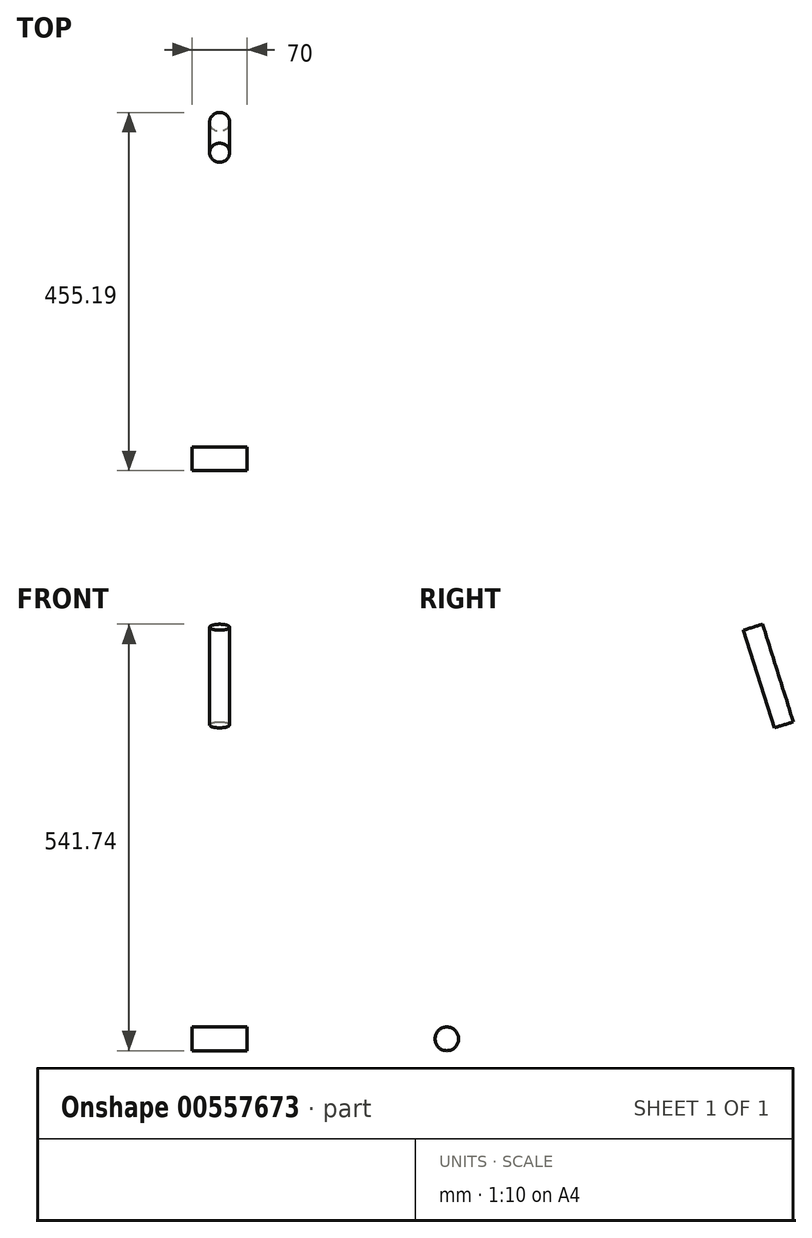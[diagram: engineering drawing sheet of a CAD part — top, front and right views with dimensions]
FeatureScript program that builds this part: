
annotation { "Feature Type Name" : "Feature", "Feature Type Description" : "" }
export const myFeature = defineFeature(function(context is Context, id is Id, definition is map)
    precondition{}
    {
        {
            var Q0;
            Q0=qCreatedBy(makeId("Right.planeOp"),FACE);
            var sketch = newSketch(context, id + "F0", { "sketchPlane" : qUnion([Q0])});
            skPoint(sketch, "E0", {"position": v(0, 271.5) * mm});
            skPoint(sketch, "E1", {"position": v(-375.23, 331.5) * mm});
            skPoint(sketch, "E2", {"position": v(576.89, 331.5) * mm});
            skCircle(sketch, "E3", {"center": v(-375.23, 331.5) * mm, "radius": 331.5 * mm});
            skCircle(sketch, "E4", {"center": v(576.89, 331.5) * mm, "radius": 331.5 * mm});
            skLineSegment(sketch, "E5", {"start": v(-873.64, 0) * mm, "end": v(1243.72, 0) * mm, "construction": true});
            skLineSegment(sketch, "E6", {"start": v(0, 0) * mm, "end": v(0, 1098.11) * mm, "construction": true});
            skLineSegment(sketch, "E7", {"start": v(-375.23, 331.5) * mm, "end": v(576.89, 331.5) * mm, "construction": true});
            skLineSegment(sketch, "E8", {"start": v(-50, 1099.43) * mm, "end": v(-50, 0) * mm, "construction": true});
            skLineSegment(sketch, "E9", {"start": v(850, 0) * mm, "end": v(850, 1102.57) * mm, "construction": true});
            skLineSegment(sketch, "E10", {"start": v(800, 0) * mm, "end": v(800, 1098.19) * mm, "construction": true});
            skLineSegment(sketch, "E11", {"start": v(750, 0) * mm, "end": v(750, 1136.17) * mm, "construction": true});
            skCircle(sketch, "E12", {"center": v(0, 271.5) * mm, "radius": 170 * mm});
            skLineSegment(sketch, "E13", {"start": v(-50, 970) * mm, "end": v(-290, 970) * mm});
            skLineSegment(sketch, "E14", {"start": v(388.99, 794.42) * mm, "end": v(639.47, 0) * mm});
            skLineSegment(sketch, "E15", {"start": v(358.03, 648.35) * mm, "end": v(482.66, 687.65) * mm});
            skPoint(sketch, "E16", {"position": v(800, 955) * mm});
            skLineSegment(sketch, "E17", {"start": v(800, 955) * mm, "end": v(454.17, 855) * mm});
            skLineSegment(sketch, "E18", {"start": v(524.17, 855) * mm, "end": v(454.17, 855) * mm});
            skLineSegment(sketch, "E19", {"start": v(477.13, 848) * mm, "end": v(547.13, 848) * mm});
            skLineSegment(sketch, "E20", {"start": v(800, 948) * mm, "end": v(477.13, 848) * mm});
            skLineSegment(sketch, "E21", {"start": v(-50, 1060) * mm, "end": v(-290, 1060) * mm});
            skPoint(sketch, "E22", {"position": v(428.08, 670.44) * mm});
            skSolve(sketch);
        }
        {
            var Q0;
            Q0=qCreatedBy(makeId("Right.planeOp"),FACE);
            var sketch = newSketch(context, id + "F1", { "sketchPlane" : qUnion([Q0])});
            skLineSegment(sketch, "E23", {"start": v(369.24, 652.29) * mm, "end": v(442.39, 684.68) * mm});
            skLineSegment(sketch, "E24", {"start": v(442.39, 684.68) * mm, "end": v(603.27, 321.3) * mm});
            skLineSegment(sketch, "E25", {"start": v(603.27, 321.3) * mm, "end": v(530.12, 288.92) * mm});
            skLineSegment(sketch, "E26", {"start": v(530.12, 288.92) * mm, "end": v(369.24, 652.29) * mm});
            skLineSegment(sketch, "E27", {"start": v(-57.53, 264) * mm, "end": v(353.83, 689.76) * mm});
            skLineSegment(sketch, "E28", {"start": v(411.37, 634.18) * mm, "end": v(353.83, 689.76) * mm});
            skLineSegment(sketch, "E29", {"start": v(411.37, 634.18) * mm, "end": v(0, 208.41) * mm});
            skLineSegment(sketch, "E30", {"start": v(0, 208.41) * mm, "end": v(-57.53, 264) * mm});
            skLineSegment(sketch, "E31", {"start": v(24.66, 216.42) * mm, "end": v(36.44, 295.55) * mm});
            skLineSegment(sketch, "E32", {"start": v(36.44, 295.55) * mm, "end": v(-430.88, 365.14) * mm});
            skLineSegment(sketch, "E33", {"start": v(-430.88, 365.14) * mm, "end": v(-442.67, 286.02) * mm});
            skLineSegment(sketch, "E34", {"start": v(-442.67, 286.02) * mm, "end": v(24.66, 216.42) * mm});
            skLineSegment(sketch, "E35", {"start": v(-97.86, 702.11) * mm, "end": v(-392.56, 270.67) * mm});
            skLineSegment(sketch, "E36", {"start": v(-458.62, 315.8) * mm, "end": v(-392.56, 270.67) * mm});
            skLineSegment(sketch, "E37", {"start": v(-163.91, 747.23) * mm, "end": v(-97.86, 702.11) * mm});
            skLineSegment(sketch, "E38", {"start": v(-163.91, 747.23) * mm, "end": v(-458.62, 315.8) * mm});
            skLineSegment(sketch, "E39", {"start": v(-19.5, 202.08) * mm, "end": v(56.58, 226.8) * mm});
            skLineSegment(sketch, "E40", {"start": v(56.58, 226.8) * mm, "end": v(-150, 862.6) * mm});
            skLineSegment(sketch, "E41", {"start": v(-150, 862.6) * mm, "end": v(-226.08, 837.87) * mm});
            skLineSegment(sketch, "E42", {"start": v(-226.08, 837.87) * mm, "end": v(-19.5, 202.08) * mm});
            skPoint(sketch, "E43.0", {"position": v(0, 271.5) * mm});
            skLineSegment(sketch, "E44", {"start": v(327, 774.88) * mm, "end": v(366.09, 650.9) * mm});
            skLineSegment(sketch, "E45", {"start": v(366.09, 650.9) * mm, "end": v(442.39, 674.95) * mm});
            skLineSegment(sketch, "E46", {"start": v(442.39, 674.95) * mm, "end": v(403.3, 798.93) * mm});
            skLineSegment(sketch, "E47", {"start": v(403.3, 798.93) * mm, "end": v(327, 774.88) * mm});
            skLineSegment(sketch, "E48.0", {"start": v(-50, 970) * mm, "end": v(-290, 970) * mm, "construction": true});
            skPoint(sketch, "E49", {"position": v(-150, 970) * mm});
            skLineSegment(sketch, "E50.bottom", {"start": v(-110, 970) * mm, "end": v(-190, 970) * mm});
            skLineSegment(sketch, "E50.top", {"start": v(-110, 782.11) * mm, "end": v(-190, 782.11) * mm});
            skLineSegment(sketch, "E50.left", {"start": v(-110, 970) * mm, "end": v(-110, 782.11) * mm});
            skLineSegment(sketch, "E50.right", {"start": v(-190, 970) * mm, "end": v(-190, 782.11) * mm});
            skPoint(sketch, "E51", {"position": v(-150, 782.11) * mm});
            skPoint(sketch, "E52.0", {"position": v(576.89, 331.5) * mm});
            skCircle(sketch, "E53", {"center": v(576.89, 331.5) * mm, "radius": 336.5 * mm, "construction": true});
            skPoint(sketch, "E54", {"position": v(387.97, 609.97) * mm});
            skPoint(sketch, "E55.0", {"position": v(-375.23, 331.5) * mm});
            skCircle(sketch, "E56", {"center": v(-375.23, 331.5) * mm, "radius": 336.5 * mm, "construction": true});
            skLineSegment(sketch, "E57", {"start": v(27.6, 236.2) * mm, "end": v(-433.83, 345.36) * mm, "construction": true});
            skPoint(sketch, "E57.startSnap0", {"position": v(-28.77, 236.2) * mm});
            skLineSegment(sketch, "E58", {"start": v(-114.37, 713.4) * mm, "end": v(-409.08, 281.96) * mm, "construction": true});
            skLineSegment(sketch, "E59", {"start": v(266.06, 702.11) * mm, "end": v(290.59, 624.3) * mm});
            skLineSegment(sketch, "E60", {"start": v(-73.13, 626.03) * mm, "end": v(-17.86, 702.11) * mm});
            skLineSegment(sketch, "E61", {"start": v(-5.9, 419.1) * mm, "end": v(74.4, 400.56) * mm});
            skLineSegment(sketch, "E62", {"start": v(-199.98, 552.6) * mm, "end": v(-130.14, 542.58) * mm});
            skLineSegment(sketch, "E63", {"start": v(-78.98, 385.14) * mm, "end": v(-133.39, 320.84) * mm});
            skPoint(sketch, "E64", {"position": v(-97.86, 702.11) * mm});
            skPoint(sketch, "E65", {"position": v(-154.86, 618.66) * mm});
            skPoint(sketch, "E66", {"position": v(-54.26, 309.06) * mm});
            skPoint(sketch, "E67", {"position": v(18.82, 343.02) * mm});
            skLineSegment(sketch, "E68.bottom", {"start": v(-123.85, 782.11) * mm, "end": v(349.94, 782.11) * mm});
            skLineSegment(sketch, "E68.top", {"start": v(-123.85, 702.11) * mm, "end": v(349.94, 702.11) * mm});
            skLineSegment(sketch, "E68.left", {"start": v(-123.85, 782.11) * mm, "end": v(-123.85, 702.11) * mm});
            skLineSegment(sketch, "E68.right", {"start": v(349.94, 782.11) * mm, "end": v(349.94, 702.11) * mm});
            skLineSegment(sketch, "E69", {"start": v(-166.7, 784.54) * mm, "end": v(-47.65, 418.16) * mm, "construction": true});
            skLineSegment(sketch, "E70", {"start": v(148.15, 476.88) * mm, "end": v(259.4, 476.88) * mm, "construction": true});
            skSolve(sketch);
        }
        {
            var Q0;
            Q0=qCreatedBy(makeId("Right.planeOp"),FACE);
            var sketch = newSketch(context, id + "F2", { "sketchPlane" : qUnion([Q0])});
            skLineSegment(sketch, "E71.0", {"start": v(-186.09, 714.78) * mm, "end": v(-425.47, 364.34) * mm});
            skLineSegment(sketch, "E72.0", {"start": v(-226.08, 837.87) * mm, "end": v(-186.09, 714.78) * mm});
            skLineSegment(sketch, "E73.0", {"start": v(-150, 862.6) * mm, "end": v(-226.08, 837.87) * mm});
            skLineSegment(sketch, "E74.0", {"start": v(403.3, 798.93) * mm, "end": v(349.94, 782.11) * mm});
            skLineSegment(sketch, "E75.0", {"start": v(439.7, 683.48) * mm, "end": v(403.3, 798.93) * mm});
            skLineSegment(sketch, "E76.0", {"start": v(442.39, 684.68) * mm, "end": v(603.27, 321.3) * mm});
            skPoint(sketch, "E77.0", {"position": v(566.7, 305.12) * mm});
            skLineSegment(sketch, "E78.0", {"start": v(603.27, 321.3) * mm, "end": v(530.12, 288.92) * mm});
            skLineSegment(sketch, "E79.0", {"start": v(530.12, 288.92) * mm, "end": v(387.97, 609.97) * mm});
            skLineSegment(sketch, "E80.0", {"start": v(387.97, 609.97) * mm, "end": v(46.81, 256.86) * mm});
            skLineSegment(sketch, "E81.0", {"start": v(-19.5, 202.08) * mm, "end": v(56.58, 226.8) * mm});
            skLineSegment(sketch, "E82.0", {"start": v(-387.68, 277.83) * mm, "end": v(-26.65, 224.06) * mm});
            skLineSegment(sketch, "E83.0", {"start": v(-458.62, 315.8) * mm, "end": v(-392.56, 270.67) * mm});
            skLineSegment(sketch, "E84.0", {"start": v(-199.98, 552.6) * mm, "end": v(-130.14, 542.58) * mm});
            skLineSegment(sketch, "E85.0", {"start": v(-78.98, 385.14) * mm, "end": v(-133.39, 320.84) * mm});
            skLineSegment(sketch, "E86.0", {"start": v(-73.13, 626.03) * mm, "end": v(-17.86, 702.11) * mm});
            skLineSegment(sketch, "E87.0", {"start": v(56.58, 226.8) * mm, "end": v(46.81, 256.86) * mm});
            skLineSegment(sketch, "E88.0", {"start": v(-5.9, 419.1) * mm, "end": v(74.4, 400.56) * mm});
            skLineSegment(sketch, "E89.0", {"start": v(266.06, 702.11) * mm, "end": v(290.59, 624.3) * mm});
            skLineSegment(sketch, "E90.trimOffspring", {"start": v(-130.14, 542.58) * mm, "end": v(-78.98, 385.14) * mm});
            skLineSegment(sketch, "E91.trimOffspring", {"start": v(-199.98, 552.6) * mm, "end": v(-337.53, 351.24) * mm});
            skPoint(sketch, "E92.0.start.orphan", {"position": v(-97.86, 702.11) * mm});
            skPoint(sketch, "E93.orphan", {"position": v(-163.91, 747.23) * mm});
            skLineSegment(sketch, "E94.trimOffspring", {"start": v(-425.47, 364.34) * mm, "end": v(-430.88, 365.14) * mm});
            skLineSegment(sketch, "E95.trimOffspring", {"start": v(-123.85, 782.11) * mm, "end": v(-150, 862.6) * mm});
            skLineSegment(sketch, "E96.trimOffspring", {"start": v(-26.65, 224.06) * mm, "end": v(-19.5, 202.08) * mm});
            skLineSegment(sketch, "E97.trimOffspring", {"start": v(-133.39, 320.84) * mm, "end": v(-337.53, 351.24) * mm});
            skLineSegment(sketch, "E98.trimOffspring", {"start": v(-5.9, 419.1) * mm, "end": v(-73.13, 626.03) * mm});
            skLineSegment(sketch, "E99.trimOffspring", {"start": v(74.4, 400.56) * mm, "end": v(290.59, 624.3) * mm});
            skPoint(sketch, "E100.orphan", {"position": v(353.83, 689.76) * mm});
            skLineSegment(sketch, "E101.0", {"start": v(-430.88, 365.14) * mm, "end": v(-432.55, 353.97) * mm});
            skLineSegment(sketch, "E102.trimOffspring", {"start": v(-387.68, 277.83) * mm, "end": v(-392.56, 270.67) * mm});
            skLineSegment(sketch, "E103.trimOffspring", {"start": v(-432.55, 353.97) * mm, "end": v(-458.62, 315.8) * mm});
            skPoint(sketch, "E104.orphan", {"position": v(-442.67, 286.02) * mm});
            skPoint(sketch, "E105.orphan", {"position": v(-57.53, 264) * mm});
            skPoint(sketch, "E106.0.start.orphan", {"position": v(36.44, 295.55) * mm});
            skPoint(sketch, "E107.trimOffspring.end.orphan", {"position": v(24.66, 216.42) * mm});
            skPoint(sketch, "E108.trimOffspring.end.orphan", {"position": v(0, 208.41) * mm});
            skPoint(sketch, "E109.orphan", {"position": v(411.37, 634.18) * mm});
            skPoint(sketch, "E110.orphan", {"position": v(369.24, 652.29) * mm});
            skLineSegment(sketch, "E111.0", {"start": v(439.7, 683.48) * mm, "end": v(442.39, 684.68) * mm});
            skPoint(sketch, "E112.orphan", {"position": v(442.39, 674.95) * mm});
            skPoint(sketch, "E113.orphan", {"position": v(327, 774.88) * mm});
            skLineSegment(sketch, "E114.0", {"start": v(-123.85, 782.11) * mm, "end": v(349.94, 782.11) * mm});
            skLineSegment(sketch, "E115.0", {"start": v(-123.85, 702.11) * mm, "end": v(-97.86, 702.11) * mm});
            skPoint(sketch, "E116.orphan", {"position": v(349.94, 702.11) * mm});
            skLineSegment(sketch, "E117.trimOffspring", {"start": v(-17.86, 702.11) * mm, "end": v(266.06, 702.11) * mm});
            skPoint(sketch, "E118.0", {"position": v(0, 0) * mm});
            skSolve(sketch);
        }
        {
            var Q0;
            Q0=sQuery(id+"F2.wireOp",EDGE,"E73.0");
            var Q1;
            Q1=sQuery(id+"F2.wireOp",EDGE,"E72.0");
            var Q2;
            Q2=sQuery(id+"F2.wireOp",EDGE,"E71.0");
            var Q3;
            Q3=sQuery(id+"F2.wireOp",EDGE,"E95.trimOffspring");
            var Q4;
            Q4=sQuery(id+"F2.wireOp",EDGE,"cf815acb-c328-4235-8576-db7b615b9363.0.5");
            var Q5;
            Q5=sQuery(id+"F2.wireOp",EDGE,"cf815acb-c328-4235-8576-db7b615b9363.0.4");
            var Q6;
            Q6=sQuery(id+"F2.wireOp",EDGE,"E74.0");
            var Q7;
            Q7=sQuery(id+"F2.wireOp",EDGE,"E75.0");
            var Q8;
            Q8=sQuery(id+"F2.wireOp",EDGE,"E111.0");
            var Q9;
            Q9=sQuery(id+"F2.wireOp",EDGE,"E76.0");
            var Q10;
            Q10=sQuery(id+"F2.wireOp",EDGE,"E78.0");
            var Q11;
            Q11=sQuery(id+"F2.wireOp",EDGE,"E79.0");
            var Q12;
            Q12=sQuery(id+"F2.wireOp",EDGE,"E80.0");
            var Q13;
            Q13=sQuery(id+"F2.wireOp",EDGE,"d12364fb-4ac9-49b3-acce-0214cc6840b1.0");
            var Q14;
            Q14=sQuery(id+"F2.wireOp",EDGE,"E87.0");
            var Q15;
            Q15=sQuery(id+"F2.wireOp",EDGE,"E81.0");
            var Q16;
            Q16=sQuery(id+"F2.wireOp",EDGE,"E96.trimOffspring");
            var Q17;
            Q17=sQuery(id+"F2.wireOp",EDGE,"E82.0");
            var Q18;
            Q18=sQuery(id+"F2.wireOp",EDGE,"E102.trimOffspring");
            var Q19;
            Q19=sQuery(id+"F2.wireOp",EDGE,"E83.0");
            var Q20;
            Q20=sQuery(id+"F2.wireOp",EDGE,"E103.trimOffspring");
            var Q21;
            Q21=sQuery(id+"F2.wireOp",EDGE,"E101.0");
            var Q22;
            Q22=sQuery(id+"F2.wireOp",EDGE,"E94.trimOffspring");
            var Q23;
            Q23=sQuery(id+"F2.wireOp",EDGE,"E97.trimOffspring");
            var Q24;
            Q24=sQuery(id+"F2.wireOp",EDGE,"E91.trimOffspring");
            var Q25;
            Q25=sQuery(id+"F2.wireOp",EDGE,"E84.0");
            var Q26;
            Q26=sQuery(id+"F2.wireOp",EDGE,"E90.trimOffspring");
            var Q27;
            Q27=sQuery(id+"F2.wireOp",EDGE,"E85.0");
            var Q28;
            Q28=sQuery(id+"F2.wireOp",EDGE,"E98.trimOffspring");
            var Q29;
            Q29=sQuery(id+"F2.wireOp",EDGE,"E86.0");
            var Q30;
            Q30=sQuery(id+"F2.wireOp",EDGE,"E88.0");
            var Q31;
            Q31=sQuery(id+"F2.wireOp",EDGE,"E99.trimOffspring");
            var Q32;
            Q32=sQuery(id+"F2.wireOp",EDGE,"E89.0");
            var Q33;
            Q33=sQuery(id+"F2.wireOp",EDGE,"cf815acb-c328-4235-8576-db7b615b9363.0.0");
            var Q34;
            Q34=sQuery(id+"F2.wireOp",EDGE,"E114.0");
            var Q35;
            Q35=sQuery(id+"F2.wireOp",EDGE,"E117.trimOffspring");
            extrude(context, id + "F3", {"bodyType" : ToolBodyType.SURFACE, "surfaceEntities" : qUnion([Q0, Q1, Q2, Q3, Q4, Q5, Q6, Q7, Q8, Q9, Q10, Q11, Q12, Q13, Q14, Q15, Q16, Q17, Q18, Q19, Q20, Q21, Q22, Q23, Q24, Q25, Q26, Q27, Q28, Q29, Q30, Q31, Q32, Q33, Q34, Q35]), "endBound" : BoundingType.SYMMETRIC, "depth" : 25 * mm, "offsetDistance" : 25 * mm});
        }
        {
            var Q0;
            Q0=qCreatedBy(makeId("Right.planeOp"),FACE);
            var sketch = newSketch(context, id + "F4", { "sketchPlane" : qUnion([Q0])});
            skPoint(sketch, "E119.0", {"position": v(-375.23, 331.5) * mm});
            skPoint(sketch, "E120.0", {"position": v(576.89, 331.5) * mm});
            skPoint(sketch, "E121.0", {"position": v(0, 271.5) * mm});
            skCircle(sketch, "E122", {"center": v(576.89, 331.5) * mm, "radius": 2.5 * mm});
            skCircle(sketch, "E123", {"center": v(-375.23, 331.5) * mm, "radius": 2.5 * mm});
            skCircle(sketch, "E124", {"center": v(0, 271.5) * mm, "radius": 15 * mm});
            skSolve(sketch);
        }
        {
            var Q0;
            Q0=sQuery(id+"F4.wireOp",EDGE,"E122");
            extrude(context, id + "F5", {"bodyType" : ToolBodyType.SURFACE, "surfaceEntities" : qUnion([Q0]), "endBound" : BoundingType.SYMMETRIC, "depth" : 65 * mm, "offsetDistance" : 25 * mm});
        }
        {
            var Q0;
            Q0=sQuery(id+"F4.wireOp",EDGE,"E123");
            extrude(context, id + "F6", {"bodyType" : ToolBodyType.SURFACE, "surfaceEntities" : qUnion([Q0]), "depth" : 50 * mm, "offsetDistance" : 25 * mm, "hasSecondDirection" : true, "secondDirectionOppositeDirection" : true, "secondDirectionDepth" : 40 * mm});
        }
        {
            var Q0;
            Q0=makeQuery(id+"F4.imprint","IMPRINT",FACE,{"disambiguationData":[TD([[makeQuery(id+"F4.imprint","IMPRINT",EDGE,{"derivedFrom":sQuery(id+"F4.wireOp",EDGE,"E124")}),1.0]])]});
            extrude(context, id + "F7", {"entities" : qUnion([Q0]), "endBound" : BoundingType.SYMMETRIC, "depth" : 70 * mm, "offsetDistance" : 25 * mm});
        }
        {
            var Q0;
            Q0=sQuery(id+"F0.wireOp",EDGE,"E14");
            var Q1;
            Q1=sQuery(id+"F0.wireOp",VERTEX,"E14.start");
            cPlane(context, id + "F8", {"entities" : qUnion([Q0, Q1]), "cplaneType" : CPlaneType.LINE_POINT, "offset" : 25 * mm, "width" : 150 * mm, "height" : 150 * mm});
        }
        {
            var Q0;
            Q0=qCreatedBy(id+"F8.planeOp",FACE);
            var sketch = newSketch(context, id + "F9", { "sketchPlane" : qUnion([Q0])});
            skCircle(sketch, "E125", {"center": v(0, -609.87) * mm, "radius": 12.7 * mm});
            skSolve(sketch);
        }
        {
            var Q0;
            Q0 = qSketchRegion(id + "F9", true);
            var Q1;
            Q1=sQuery(id+"F0.wireOp",VERTEX,"E22");
            extrude(context, id + "F10", {"entities" : qUnion([Q0]), "endBound" : BoundingType.UP_TO_VERTEX, "depth" : 25 * mm, "endBoundEntityVertex" : qUnion([Q1]), "offsetDistance" : 25 * mm});
        }
        {
            var Q0;
            Q0=qCreatedBy(makeId("Right.planeOp"),FACE);
            var sketch = newSketch(context, id + "F11", { "sketchPlane" : qUnion([Q0])});
            skLineSegment(sketch, "E126.bottom", {"start": v(493.3, 775.13) * mm, "end": v(573.3, 775.13) * mm});
            skLineSegment(sketch, "E126.top", {"start": v(493.3, 750.13) * mm, "end": v(573.3, 750.13) * mm});
            skLineSegment(sketch, "E126.left", {"start": v(493.3, 775.13) * mm, "end": v(493.3, 750.13) * mm});
            skLineSegment(sketch, "E126.right", {"start": v(573.3, 775.13) * mm, "end": v(573.3, 750.13) * mm});
            skSolve(sketch);
        }
        {
            var Q0;
            Q0 = qSketchRegion(id + "F11", true);
            var Q1;
            Q1=sQuery(id+"F11.wireOp",EDGE,"E126.top");
            var Q2;
            Q2=sQuery(id+"F11.wireOp",EDGE,"E126.right");
            var Q3;
            Q3=sQuery(id+"F11.wireOp",EDGE,"E126.bottom");
            var Q4;
            Q4=sQuery(id+"F11.wireOp",EDGE,"E126.left");
            extrude(context, id + "F12", {"entities" : qUnion([Q0]), "bodyType" : ToolBodyType.SURFACE, "surfaceEntities" : qUnion([Q1, Q2, Q3, Q4]), "endBound" : BoundingType.SYMMETRIC, "depth" : 280 * mm, "offsetDistance" : 25 * mm});
        }
    });
